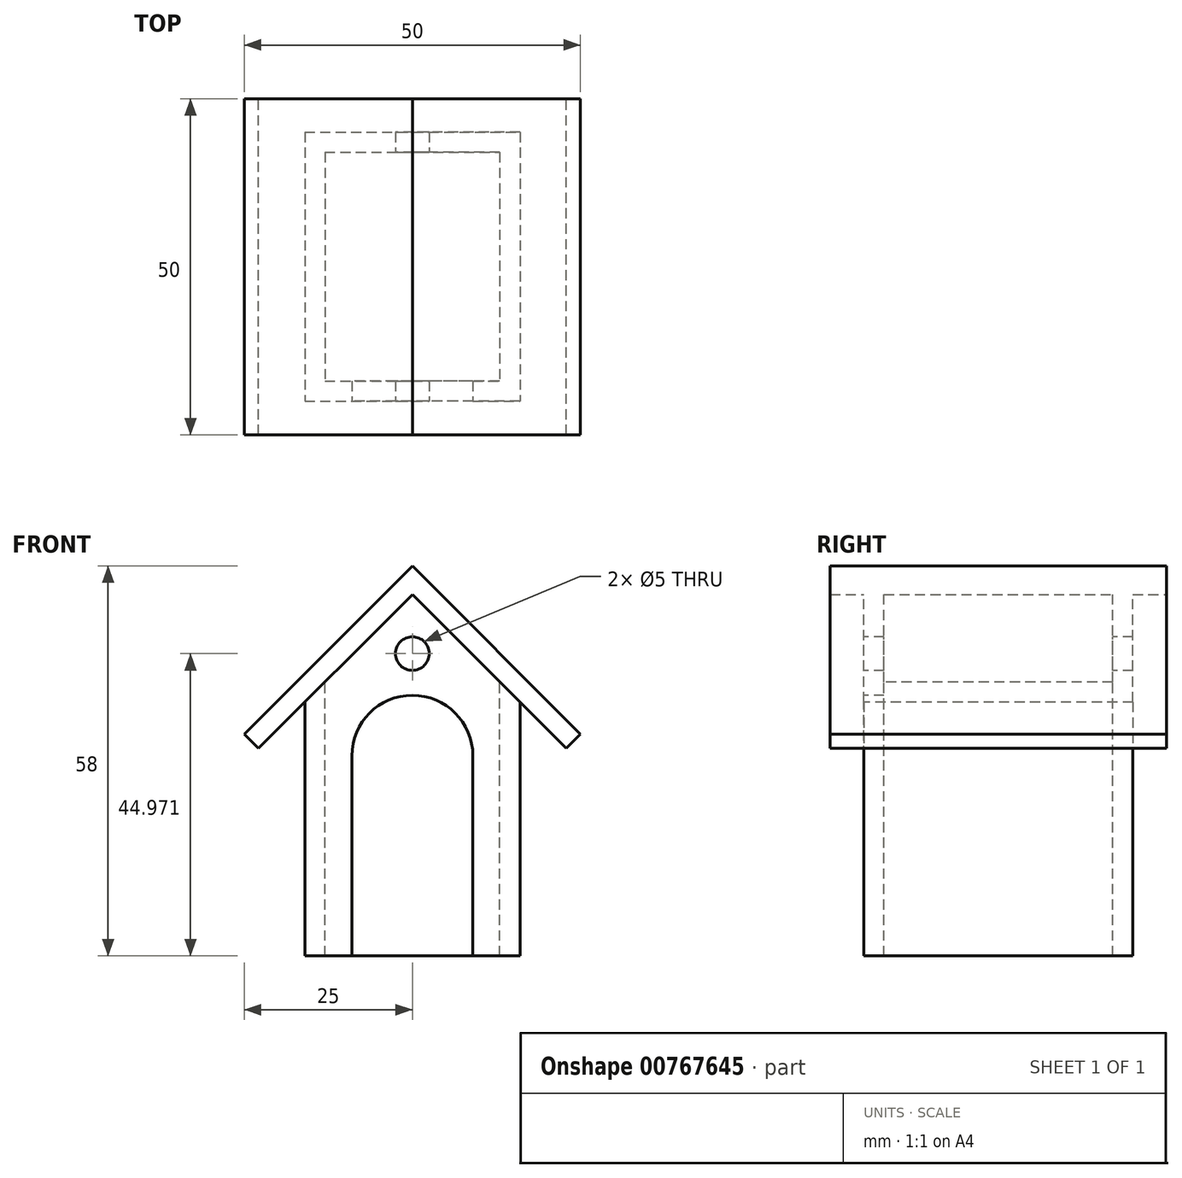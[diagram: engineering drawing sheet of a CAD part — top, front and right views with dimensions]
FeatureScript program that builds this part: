
annotation { "Feature Type Name" : "Feature", "Feature Type Description" : "" }
export const myFeature = defineFeature(function(context is Context, id is Id, definition is map)
    precondition{}
    {
        {
            var Q0;
            Q0=qCreatedBy(makeId("Front.planeOp"),FACE);
            var sketch = newSketch(context, id + "F0", { "sketchPlane" : qUnion([Q0])});
            skLineSegment(sketch, "E0", {"start": v(0, 0) * mm, "end": v(0, 60) * mm, "construction": true});
            skLineSegment(sketch, "E1", {"start": v(0, 60) * mm, "end": v(25, 35) * mm});
            skLineSegment(sketch, "E2", {"start": v(25, 35) * mm, "end": v(22.88, 32.88) * mm});
            skLineSegment(sketch, "E3", {"start": v(22.88, 32.88) * mm, "end": v(0, 55.76) * mm});
            skLineSegment(sketch, "E4", {"start": v(16, 39.76) * mm, "end": v(16, 0) * mm});
            skLineSegment(sketch, "E5", {"start": v(16, 0) * mm, "end": v(0, 0) * mm});
            skLineSegment(sketch, "E6.MirrorCS", {"start": v(0, 60) * mm, "end": v(-25, 35) * mm});
            skLineSegment(sketch, "E7.MirrorCS", {"start": v(-22.88, 32.88) * mm, "end": v(0, 55.76) * mm});
            skLineSegment(sketch, "E8.MirrorCS", {"start": v(-16, 39.76) * mm, "end": v(-16, 0) * mm});
            skLineSegment(sketch, "E9.MirrorCS", {"start": v(-25, 35) * mm, "end": v(-22.88, 32.88) * mm});
            skLineSegment(sketch, "E10.MirrorCS", {"start": v(-16, 0) * mm, "end": v(0, 0) * mm});
            skLineSegment(sketch, "E11", {"start": v(9, 0) * mm, "end": v(9, 31.76) * mm});
            skArc(sketch, "E12", {"start": v(9, 31.76) * mm, "mid": v(0, 40.76) * mm, "end": v(-9, 31.76) * mm});
            skLineSegment(sketch, "E13.MirrorCS", {"start": v(-9, 0) * mm, "end": v(-9, 31.76) * mm});
            skLineSegment(sketch, "E14", {"start": v(13, 0) * mm, "end": v(13, 42.76) * mm});
            skLineSegment(sketch, "E15.MirrorCS", {"start": v(-13, 0) * mm, "end": v(-13, 42.76) * mm});
            skCircle(sketch, "E16", {"center": v(0, 46.97) * mm, "radius": 2.5 * mm});
            skLineSegment(sketch, "E17", {"start": v(0, 46.97) * mm, "end": v(-4.4, 51.36) * mm, "construction": true});
            skLineSegment(sketch, "E18", {"start": v(0, 46.97) * mm, "end": v(4.4, 51.36) * mm, "construction": true});
            skLineSegment(sketch, "E19", {"start": v(0, 46.97) * mm, "end": v(0, 40.76) * mm, "construction": true});
            skLineSegment(sketch, "E20", {"start": v(-16, 2) * mm, "end": v(16, 2) * mm});
            skSolve(sketch);
        }
        {
            var Q0;
            {var subQ0=sQuery(id+"F0.wireOp",EDGE,"E8.MirrorCS");var subQ1=sQuery(id+"F0.wireOp",EDGE,"E7.MirrorCS");var subQ2=makeQuery(id+"F0.imprint","INTERSECT",VERTEX,{"derivedFrom":[subQ1,subQ0]});Q0=makeQuery(id+"F0.imprint","IMPRINT",FACE,{"disambiguationData":[TD([[makeQuery(id+"F0.imprint","IMPRINT",EDGE,{"disambiguationData":[TD([[subQ2,-1.0]])],"derivedFrom":subQ1}),-1.0]])]});}
            var Q1;
            {var subQ0=sQuery(id+"F0.wireOp",EDGE,"E12");Q1=makeQuery(id+"F0.imprint","IMPRINT",FACE,{"disambiguationData":[TD([[makeQuery(id+"F0.imprint","IMPRINT",EDGE,{"derivedFrom":subQ0}),-1.0]])]});}
            var Q2;
            {var subQ0=sQuery(id+"F0.wireOp",EDGE,"E4");var subQ1=sQuery(id+"F0.wireOp",EDGE,"E3");var subQ2=makeQuery(id+"F0.imprint","INTERSECT",VERTEX,{"derivedFrom":[subQ1,subQ0]});Q2=makeQuery(id+"F0.imprint","IMPRINT",FACE,{"disambiguationData":[TD([[makeQuery(id+"F0.imprint","IMPRINT",EDGE,{"disambiguationData":[TD([[subQ2,-1.0]])],"derivedFrom":subQ1}),1.0]])]});}
            extrude(context, id + "F1", {"entities" : qUnion([Q0, Q1, Q2]), "oppositeDirection" : true, "depth" : 3 * mm, "offsetDistance" : 25 * mm});
        }
        {
            var Q0;
            Q0=makeQuery(id+"F0.imprint","IMPRINT",FACE,{"disambiguationData":[TD([[makeQuery(id+"F0.imprint","IMPRINT",EDGE,{"derivedFrom":sQuery(id+"F0.wireOp",EDGE,"E1")}),-1.0]])]});
            extrude(context, id + "F2", {"entities" : qUnion([Q0]), "operationType" : NewBodyOperationType.ADD, "depth" : 5 * mm, "offsetDistance" : 25 * mm, "hasSecondDirection" : true, "secondDirectionOppositeDirection" : true, "secondDirectionDepth" : 45 * mm});
        }
        {
            var Q0;
            {var subQ0=sQuery(id+"F0.wireOp",EDGE,"E8.MirrorCS");var subQ1=sQuery(id+"F0.wireOp",EDGE,"E7.MirrorCS");var subQ2=makeQuery(id+"F0.imprint","INTERSECT",VERTEX,{"derivedFrom":[subQ1,subQ0]});Q0=makeQuery(id+"F0.imprint","IMPRINT",FACE,{"disambiguationData":[TD([[makeQuery(id+"F0.imprint","IMPRINT",EDGE,{"disambiguationData":[TD([[subQ2,-1.0]])],"derivedFrom":subQ1}),-1.0]])]});}
            var Q1;
            {var subQ0=sQuery(id+"F0.wireOp",EDGE,"E4");var subQ1=sQuery(id+"F0.wireOp",EDGE,"E3");var subQ2=makeQuery(id+"F0.imprint","INTERSECT",VERTEX,{"derivedFrom":[subQ1,subQ0]});Q1=makeQuery(id+"F0.imprint","IMPRINT",FACE,{"disambiguationData":[TD([[makeQuery(id+"F0.imprint","IMPRINT",EDGE,{"disambiguationData":[TD([[subQ2,-1.0]])],"derivedFrom":subQ1}),1.0]])]});}
            extrude(context, id + "F3", {"entities" : qUnion([Q0, Q1]), "operationType" : NewBodyOperationType.ADD, "oppositeDirection" : true, "depth" : 40 * mm, "offsetDistance" : 25 * mm});
        }
        {
            var Q0;
            {var subQ0=sQuery(id+"F0.wireOp",EDGE,"E12");Q0=makeQuery(id+"F0.imprint","IMPRINT",FACE,{"disambiguationData":[TD([[makeQuery(id+"F0.imprint","IMPRINT",EDGE,{"derivedFrom":subQ0}),-1.0]])]});}
            var Q1;
            {var subQ0=sQuery(id+"F0.wireOp",EDGE,"E12");Q1=makeQuery(id+"F0.imprint","IMPRINT",FACE,{"disambiguationData":[TD([[makeQuery(id+"F0.imprint","IMPRINT",EDGE,{"derivedFrom":subQ0}),1.0]])]});}
            extrude(context, id + "F4", {"entities" : qUnion([Q0, Q1]), "operationType" : NewBodyOperationType.ADD, "oppositeDirection" : true, "depth" : 40 * mm, "offsetDistance" : 25 * mm, "hasSecondDirection" : true, "secondDirectionOppositeDirection" : true, "secondDirectionDepth" : 37 * mm});
        }
    });
